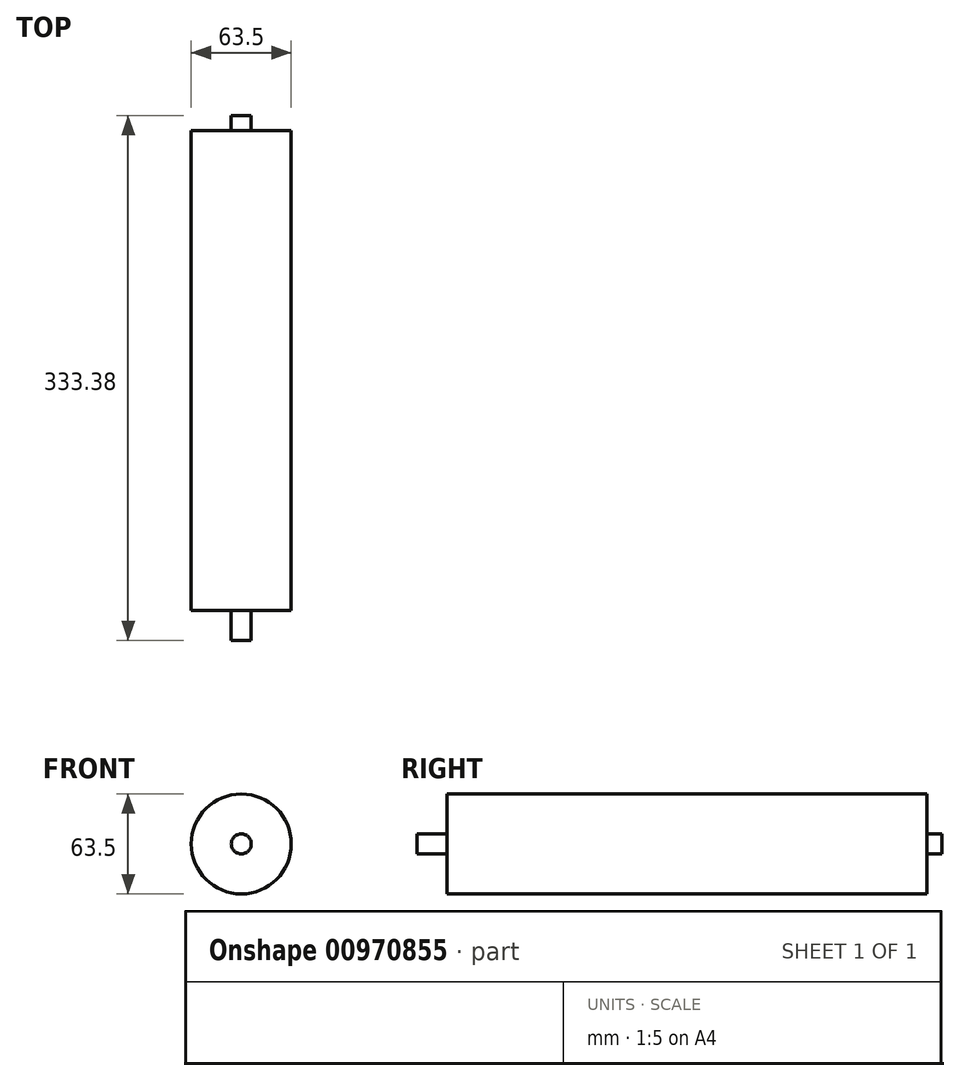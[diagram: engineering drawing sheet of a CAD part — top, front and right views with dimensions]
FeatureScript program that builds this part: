
annotation { "Feature Type Name" : "Feature", "Feature Type Description" : "" }
export const myFeature = defineFeature(function(context is Context, id is Id, definition is map)
    precondition{}
    {
        {
            var Q0;
            Q0=qCreatedBy(makeId("Front.planeOp"),FACE);
            var sketch = newSketch(context, id + "F0", { "sketchPlane" : qUnion([Q0])});
            skCircle(sketch, "E0", {"center": v(-74.68, 45.86) * mm, "radius": 31.75 * mm});
            skSolve(sketch);
        }
        {
            var Q0;
            Q0=makeQuery(id+"F0.imprint","IMPRINT",FACE,{"disambiguationData":[TD([[makeQuery(id+"F0.imprint","IMPRINT",EDGE,{"derivedFrom":sQuery(id+"F0.wireOp",EDGE,"E0")}),1.0]])]});
            extrude(context, id + "F1", {"entities" : qUnion([Q0]), "depth" : 304.8 * mm, "offsetDistance" : 25.4 * mm});
        }
        {
            var Q0;
            Q0=makeQuery(id+"F1.opExtrude","CAP_FACE",FACE,{"disambiguationData":[OSD([sQuery(id+"F0.wireOp",EDGE,"E0")])],"isStart":true});
            var sketch = newSketch(context, id + "F2", { "sketchPlane" : qUnion([Q0])});
            skCircle(sketch, "E1", {"center": v(74.68, 45.86) * mm, "radius": 6.35 * mm});
            skSolve(sketch);
        }
        {
            var Q0;
            Q0=makeQuery(id+"F2.imprint","IMPRINT",FACE,{"disambiguationData":[TD([[makeQuery(id+"F2.imprint","IMPRINT",EDGE,{"derivedFrom":sQuery(id+"F2.wireOp",EDGE,"E1")}),1.0]])]});
            extrude(context, id + "F3", {"entities" : qUnion([Q0]), "operationType" : NewBodyOperationType.ADD, "depth" : 19.05 * mm, "offsetDistance" : 25.4 * mm, "symmetric" : true});
        }
        {
            var Q0;
            Q0=makeQuery(id+"F1.opExtrude","CAP_FACE",FACE,{"disambiguationData":[OSD([sQuery(id+"F0.wireOp",EDGE,"E0")])],"isStart":false});
            var sketch = newSketch(context, id + "F4", { "sketchPlane" : qUnion([Q0])});
            skCircle(sketch, "E2", {"center": v(-74.68, 45.86) * mm, "radius": 6.35 * mm});
            skSolve(sketch);
        }
        {
            var Q0;
            Q0=makeQuery(id+"F4.imprint","IMPRINT",FACE,{"disambiguationData":[TD([[makeQuery(id+"F4.imprint","IMPRINT",EDGE,{"derivedFrom":sQuery(id+"F4.wireOp",EDGE,"E2")}),1.0]])]});
            extrude(context, id + "F5", {"entities" : qUnion([Q0]), "operationType" : NewBodyOperationType.ADD, "depth" : 19.05 * mm, "offsetDistance" : 25.4 * mm});
        }
    });
